# Revit family: IP 900_50_D
name_source: partatom
category: Mechanical Equipment
revit_build: Autodesk Revit 2018 (Build: 20170223_1515(x64)
units: mm (PartAtom-declared; Revit-internal decimal feet)

## family parameters
Always vertical = Yes
Cut with Voids When Loaded = No
Part Type = Normal
Room Calculation Point = No
Round Connector Dimension = Use Radius
Shared = No
Work Plane-Based = No

## types (2) — shared parameters
Cable Length (m) = 10
Capacity(m3/hr) = 18 m³
Description = The IP 900 is a high-grade stainless steel pump for aggressive
media. Vortex hydraulics with 30 mm free passage make it
particularly suitable for the pumping of fluids containing
gaseous or abrasive particles.
Head(m) = 12 mm  [stored 0.0393701 ft]
Impeller = Stainless steel 1.4401 (AISI 316)
Manufacturer = Sulzer
Mechanical Seal = Silicon Carbide
Model = Light Drainage Pump Type ABS IP 900
Motor Cable = PVC
Motor Housing = Stainless steel 1.4401 (AISI 316)
Other Seals = Viton
Product Specification Link = https://www.sulzer.com

## per-type parameters (varying)
| type | Cable Type (H05V V-F) | Motor Power (kW) | Rated Current (A) | Rated Voltage (V) |
| IP 900 D | 4G1.0 | P1=1.4 P2=1.1 | 2.4 | 400 3~ |
| IP 900 W | 3G1.0 | P1=1.5 P2=1.1 | 6.6 | 220-240 1~ |

note: [stored X ft] marks values corroborated as IEEE doubles in the binary element streams (Revit-internal decimal feet)

## geometry (parser evidence)
native form markers: Sweep x3
no freeform markers — native parametric forms only
